# Revit family: Hager-WITTY ONE ON PEDESTAL-nl-BE-BE
name_source: partatom
category: Electrical Fixtures
units: mm (PartAtom-declared; Revit-internal decimal feet)

## family parameters
Always vertical = Yes
Cut with Voids When Loaded = No
Maintain Annotation Orientation = No
Part Type = Normal
Room Calculation Point = No
Round Connector Dimension = Use Diameter
Shared = No
Work Plane-Based = No

## types (4) — shared parameters
BC_METADATA = {"ObjectGuid":"309c69a2-f6b5-4723-8d44-322179afe64e","ModelGuid":"04826155-e6fb-4358-826f-cf700e871803","VariantGuid":"d0dc6e8a-84e1-41b3-adf0-62c97217fd0d","Revision":"#2","VariantName":"REF 1"}
BC_MODEL_ID = 1528348
BC_OBJECT_ID = 511103
BC_OBJECT_VERSION = #1
Code hager = ADD_EC002883_ECVS_WO
EF000003 - Montagewijze = Wandmontage
EF000008 - Breedte = 250 mm  [stored 0.82021 ft]
EF000040 - Hoogte = 370 mm  [stored 1.21391 ft]
EF000049 - Diepte = 150 mm
EF000458 - Met display = No
EF001596 - Materiaal behuizing = Kunststof
EF002136 - Nominaal aansluitvermogen = 11000 W
EF003840 - Ingangsspanning = 400 V
EF004293 - Slagvastheid = IK08
EF005455 - Frequentie = 50/60 Hz
EF005474 - Beschermingsgraad (IP) = IP54
EF007001 - Uitgangsspanning bij DC = 0 V
EF007353 - Maxi. uitgangsstroom bij DC = 0 A
EF009078 - Aantal laadpunten = 1
EF009089 - Met huishoudelijke aansluitkast (HAK) = No
EF009300 - Max. vermogen per laadpunt = 11000 W
EF009313 - Met energieteller, energiemeter = No
EF009314 - Met vermogenschakelaar = No
EF009547 - LTE = No
EF011072 - Met IFTTT ondersteuning = No
EF012191 - Met ingebouwde RFID-kaartlezer = Yes
EF012361 - NFC (Near Field Communication) = No
EF013154 - Verbinding via WLAN = No
EF014925 - Compatible met Apple HomeKit = No
EF014926 - Compatible met Google Assistant = No
EF014927 - Compatible met Amazon Alexa = No
EF016385 - Mobiele communicatiestandaard 5G = No
EF017508 - Geschikt voor netwerken als master = No
EF017509 - DC reststroomdetectie = Yes
EF017510 - Lasdetectie van schakelaars = Yes
EF017511 - Met sleutelschakelaar = No
EF017512 - Export van oplaadlogs = Yes
EF017513 - Open Charge Point Protocol (OCPP) versie = 1.6
EF017515 - Plug and charge (ISO 15118) = No
EF017517 - Geschikt voor netwerken als uitbreiding = No
EF017663 - Laadkabel permanent vergrendelbaar op laadapparaat = Yes
EF017664 - In netwerk op te nemen via LAN = No
EF017665 - Met MID-compatibele energiemeter = No
EF017668 - Statisch belastingmanagement geïntegreerd = No
EF017669 - Geschikt voor dynamisch belastingmanagement = Yes
EF017672 - Backend meegeleverd = No
EF017972 - Bediening en configuratie per app = Yes
EF025053 - Uitvoering aansluiting installatiezijde = 3-fasig
EFDE0066 - Conform de kalibratiewet = No
ETIM class code = EC002883
ETIM class name = Charging device E-Mobility
HG000003-Range = WITTY ONE
HG000065-With socket TE = No
HG000099-Onfly Template ID = WittyOne_EVCS_On_Pedestal
Manufacturer = hager France
Name = WITTY ONE ON PEDESTAL-BE
Name BIM&CO = Electricity
Name hager = ADD_ChargingStation_EC002883
Reference description = ECVS Witty 1x11kW 3P T2S
zero-valued in all types: Default Elevation, EF008200 - Aansluitbare geleiderdoorsnede, EF009091 - Aantal FI-schakelaars type A, EF009092 - Aantal FI-schakelaars type B, EF009301 - Aantal oplaadkoppelingen type 1, EF009302 - Aantal oplaadkoppelingen type 1 CCS, EF009303 - Aantal oplaadkoppelingen type 2, EF009304 - Aantal oplaadkoppelingen type 2 CCS, EF009306 - Aantal oplaadkoppelingen type GB AC, EF009307 - Aantal oplaadkoppelingen type GB DC, EF009310 - Aantal oplaadkoppelingen CHAdeMO, EF009311 - Aantal huishoudelijke stopcontacten

## per-type parameters (varying)
| type | BC_VARIANT_ID | EF014895 - Lengte van de laadkabel | HG000004-Manufacturer reference |
| WITTY ONE-1x11kW-3P-XVR111S-DOUBLE STATION-RECTANGULAR PEDESTAL | 1164397 | 0 mm  [stored 0 ft] | XVR111S / XVR111S / XVA135 |
| WITTY ONE-1x11kW-3P-XVR111S-RECTANGULAR PEDESTAL | 1164401 | 0 mm  [stored 0 ft] | XVR111S / XVA130 |
| WITTY ONE-1x11kW-3P-XVR111C-RECTANGULAR PEDESTAL | 1164402 | 6500 mm  [stored 21.3255 ft] | XVR111C / XVA130 |
| WITTY ONE-1x11kW-3P-XVR111C-DOUBLE STATION-RECTANGULAR PEDESTAL | 1164403 | 6500 mm  [stored 21.3255 ft] | XVR111C / XVR111C / XVA135 |

note: column(s) folded — value = type name in every type: Reference

note: [stored X ft] marks values corroborated as IEEE doubles in the binary element streams (Revit-internal decimal feet)
